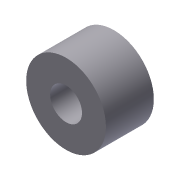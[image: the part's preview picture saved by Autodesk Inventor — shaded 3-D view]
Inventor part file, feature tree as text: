
AUTODESK INVENTOR PART (.ipt)
format: ipt  version: 2012 (Build 160160000, 160)  size: 77,824 bytes
history: native  units: in
note: dims shown in document units (in); Inventor stores cm internally (conversion verified against a paired STEP export)
features: extrude x1, sketch x1
ambient origin geometry x8: Origin, YZ Plane, XZ Plane, XY Plane, X Axis, Y Axis, Z Axis, Center Point
bodies: Solid1 (feature_tree)
feature tree (2):
  extrude  "Extrusion1"  Depth=0.25in
  sketch  "Sketch1"  dims[d0=0.625in d1=0.25in d2=0.375in d3=0.0in]
